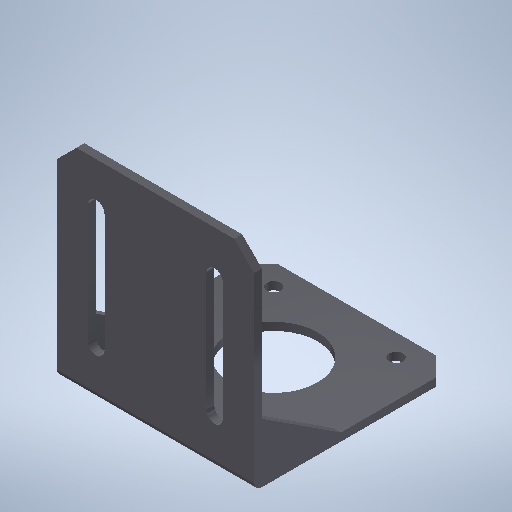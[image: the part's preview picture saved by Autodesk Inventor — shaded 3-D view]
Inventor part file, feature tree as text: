
AUTODESK INVENTOR PART (.ipt)
format: ipt  version: 2025.1 (Build 291241000, 241)  size: 316,416 bytes
history: native  units: mm
features: sketch x5, extrude x3, fillet x2, other x1, pattern_linear x1, hole x1
ambient origin geometry x8: Origin, YZ Plane, XZ Plane, XY Plane, X Axis, Y Axis, Z Axis, Center Point
bodies: Body1 (feature_tree)
feature tree (13):
  other  "Sólido1"
  sketch  "Boceto1"  dims[d0=50.0mm d1=51.0mm]
  extrude  "Extrusión1"  Depth=51.0mm
  extrude  "Extrusión2"  Depth=22.1mm
  extrude  "Extrusión3"  Depth=5.0mm
  pattern_linear  "Patrón rectangular1"  Spacing1=2.0mm  [1 undecoded]
  fillet  "Empalme1"  Radius=53.0mm
  fillet  "Empalme2"  Radius=4.2mm
  hole  "Hole1"  [1 undecoded]
  sketch  "Boceto2"  dims[d15=5.0mm d16=5.0mm]
  sketch  "Esboço - Padrão retangular1"  dims[d2=21.0mm d3=22.1mm]
  sketch  "Boceto3"  dims[d18=5.0mm d19=2.0mm d20=0.0mm d21=53.0mm d24=4.2mm d25=7.9mm d26=2.1mm d27=2.1mm d28=20.0mm d30=30.0mm d31=10.0mm d33=10.0mm d35=2.0mm d36=0.0mm d37=5.0mm d38=5.0mm d39=5.0mm d40=5.0mm d41=20.0mm d42=13.0mm d43=2.0mm d44=0.0mm d45=20.0mm d47=48.0mm d48=2.0mm d49=2.0mm d50=15.5mm d51=15.5mm d52=20.0mm d54=31.0mm d55=20.0mm d57=31.0mm d60=3.5mm d61=6.0mm d62=3.023mm d63=2.0mm d64=14.3117mm d65=8.0mm d66=20.594885mm d67=30.0mm d68=11.0mm]
  sketch  "Esboço - Padrão retangular2"  dims[d17=5.0mm]
note: 2 required parameter values undecoded (feature->parameter linkage not recoverable at this tier; creation-order binding heuristic only, values carry confidence <= 0.55)
